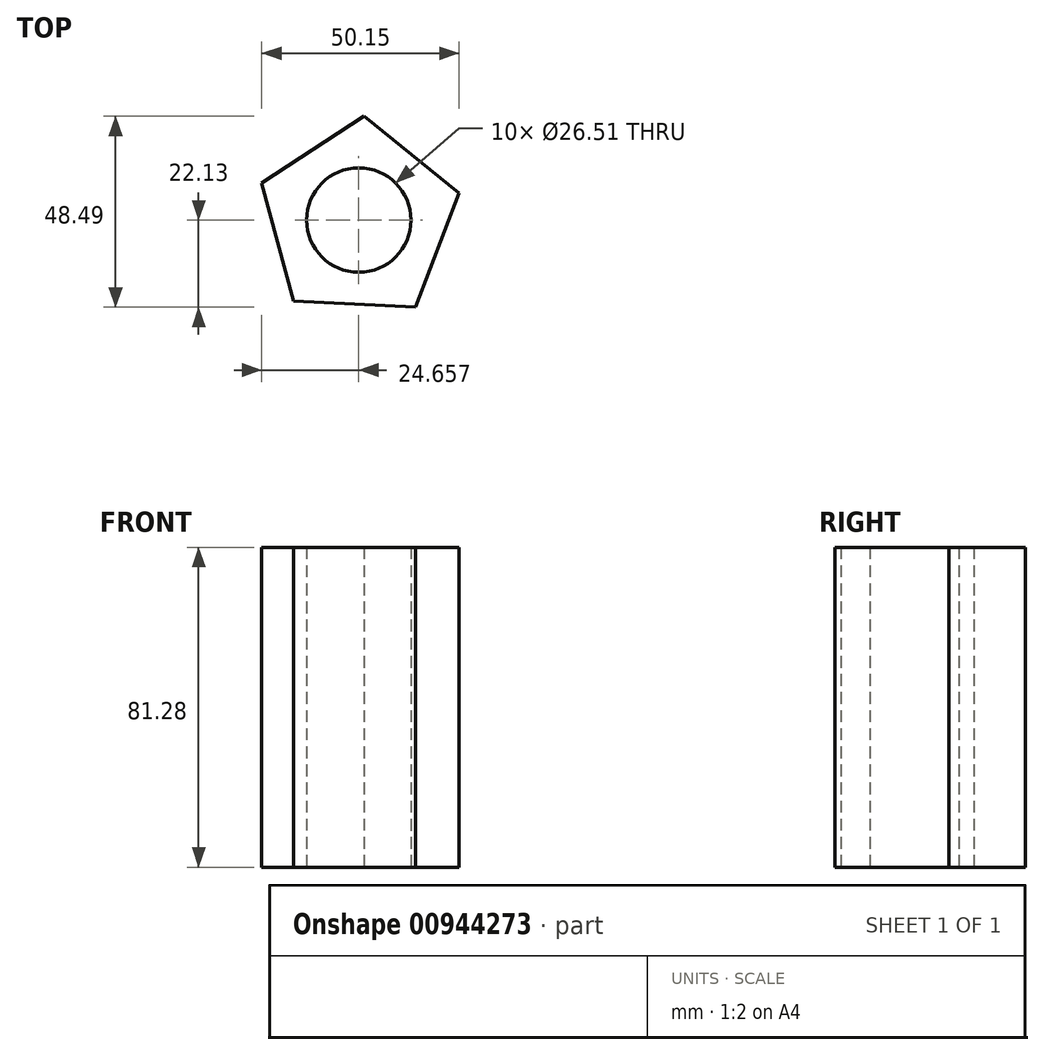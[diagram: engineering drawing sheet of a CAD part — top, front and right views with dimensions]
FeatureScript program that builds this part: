
annotation { "Feature Type Name" : "Feature", "Feature Type Description" : "" }
export const myFeature = defineFeature(function(context is Context, id is Id, definition is map)
    precondition{}
    {
        {
            var Q0;
            Q0=qCreatedBy(makeId("Front.planeOp"),FACE);
            var sketch = newSketch(context, id + "F0", { "sketchPlane" : qUnion([Q0])});
            skLineSegment(sketch, "E0", {"start": v(0, 46.55) * mm, "end": v(0, -42.35) * mm});
            skLineSegment(sketch, "E1", {"start": v(0, 46.55) * mm, "end": v(13.43, 46.55) * mm});
            skLineSegment(sketch, "E2", {"start": v(13.43, 46.55) * mm, "end": v(13.43, -42.35) * mm});
            skLineSegment(sketch, "E3", {"start": v(13.43, -42.35) * mm, "end": v(0, -42.35) * mm});
            skSolve(sketch);
        }
        {
            var Q0;
            Q0=sQuery(id+"F0.wireOp",EDGE,"E0");
            var Q1;
            Q1=sQuery(id+"F0.wireOp",EDGE,"E2");
            revolve(context, id + "F1", {"bodyType" : ToolBodyType.SURFACE, "surfaceOperationType" : NewSurfaceOperationType.NEW, "surfaceEntities" : qUnion([Q0]), "axis" : qUnion([Q1]), "revolveType" : RevolveType.FULL});
        }
        {
            var Q0;
            Q0=qCreatedBy(makeId("Front.planeOp"),FACE);
            var sketch = newSketch(context, id + "F2", { "sketchPlane" : qUnion([Q0])});
            skLineSegment(sketch, "E4", {"start": v(39.66, 46.71) * mm, "end": v(-13.73, 46.71) * mm});
            skLineSegment(sketch, "E5", {"start": v(-13.73, 46.71) * mm, "end": v(-13.73, -42.5) * mm});
            skLineSegment(sketch, "E6", {"start": v(-13.73, -42.5) * mm, "end": v(39.66, -42.5) * mm});
            skLineSegment(sketch, "E7", {"start": v(39.66, -42.5) * mm, "end": v(39.66, 46.71) * mm});
            skSolve(sketch);
        }
        {
            var Q0;
            Q0=sQuery(id+"F2.wireOp",EDGE,"E7");
            var Q1;
            Q1=sQuery(id+"F0.wireOp",EDGE,"E2");
            revolve(context, id + "F3", {"bodyType" : ToolBodyType.SURFACE, "surfaceOperationType" : NewSurfaceOperationType.NEW, "surfaceEntities" : qUnion([Q0]), "axis" : qUnion([Q1]), "revolveType" : RevolveType.FULL});
        }
        {
            var Q0;
            Q0=qCreatedBy(makeId("Top.planeOp"),FACE);
            var sketch = newSketch(context, id + "F4", { "sketchPlane" : qUnion([Q0])});
            skCircle(sketch, "E8.cCircle", {"center": v(13.26, 0) * mm, "radius": 26.4 * mm, "construction": true});
            skLineSegment(sketch, "E8.0", {"start": v(-3.34, -20.53) * mm, "end": v(-11.4, 9.44) * mm});
            skLineSegment(sketch, "E8.1", {"start": v(-11.4, 9.44) * mm, "end": v(14.62, 26.36) * mm});
            skLineSegment(sketch, "E8.2", {"start": v(14.62, 26.36) * mm, "end": v(38.75, 6.85) * mm});
            skLineSegment(sketch, "E8.3", {"start": v(38.75, 6.85) * mm, "end": v(27.65, -22.13) * mm});
            skLineSegment(sketch, "E8.4", {"start": v(27.65, -22.13) * mm, "end": v(-3.34, -20.53) * mm});
            skCircle(sketch, "E9", {"center": v(13.26, 0) * mm, "radius": 13.26 * mm});
            skSolve(sketch);
        }
        {
            var Q0;
            Q0=makeQuery(id+"F4.imprint","IMPRINT",FACE,{"disambiguationData":[TD([[makeQuery(id+"F4.imprint","IMPRINT",EDGE,{"derivedFrom":sQuery(id+"F4.wireOp",EDGE,"E8.0")}),-1.0]])]});
            extrude(context, id + "F5", {"entities" : qUnion([Q0]), "endBound" : BoundingType.SYMMETRIC, "depth" : 81.28 * mm, "offsetDistance" : 25.4 * mm});
        }
    });
